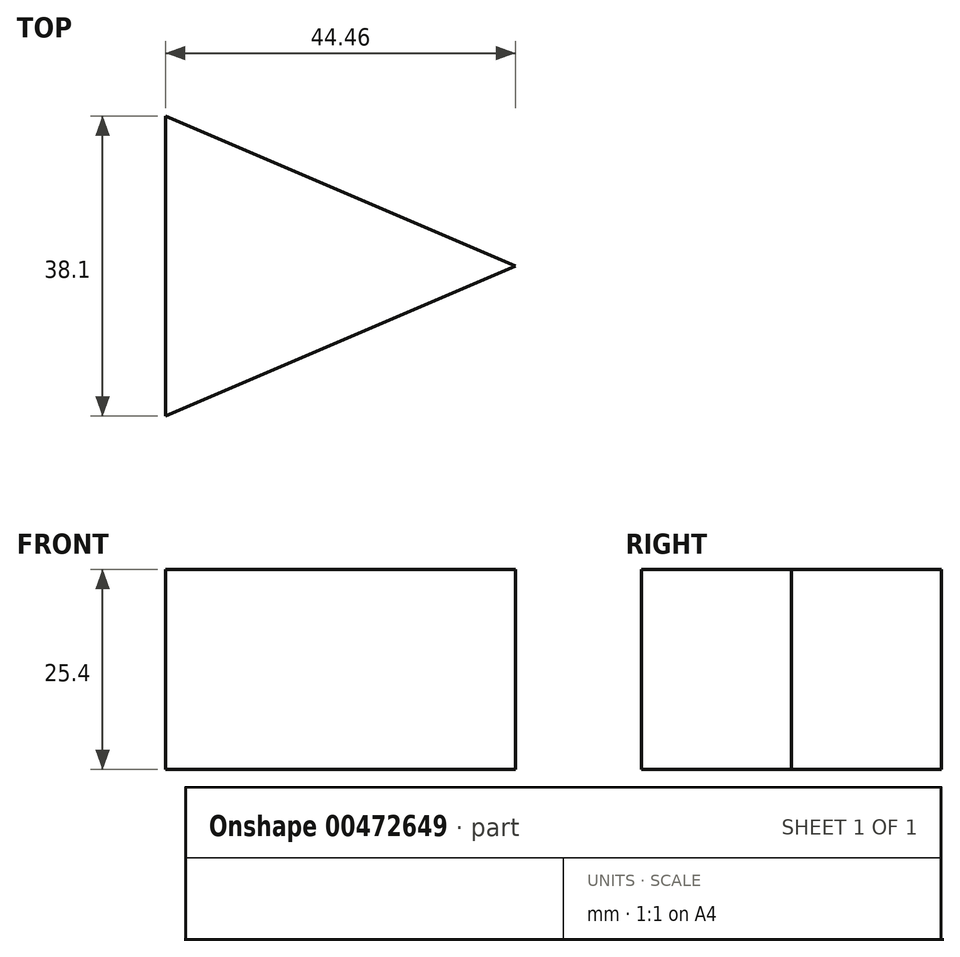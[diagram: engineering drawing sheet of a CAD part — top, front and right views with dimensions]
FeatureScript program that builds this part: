
annotation { "Feature Type Name" : "Feature", "Feature Type Description" : "" }
export const myFeature = defineFeature(function(context is Context, id is Id, definition is map)
    precondition{}
    {
        {
            var Q0;
            Q0=qCreatedBy(makeId("Top.planeOp"),FACE);
            var sketch = newSketch(context, id + "F0", { "sketchPlane" : qUnion([Q0])});
            skLineSegment(sketch, "E0", {"start": v(-22.23, 19.05) * mm, "end": v(22.23, 0) * mm});
            skLineSegment(sketch, "E1", {"start": v(22.23, 0) * mm, "end": v(-22.23, -19.05) * mm});
            skLineSegment(sketch, "E2", {"start": v(-22.23, -19.05) * mm, "end": v(-22.23, 19.05) * mm});
            skSolve(sketch);
        }
        {
            var Q0;
            Q0=makeQuery(id+"F0.imprint","IMPRINT",FACE,{"disambiguationData":[TD([[makeQuery(id+"F0.imprint","IMPRINT",EDGE,{"derivedFrom":sQuery(id+"F0.wireOp",EDGE,"E0")}),-1.0]])]});
            extrude(context, id + "F1", {"entities" : qUnion([Q0]), "depth" : 25.4 * mm});
        }
    });
